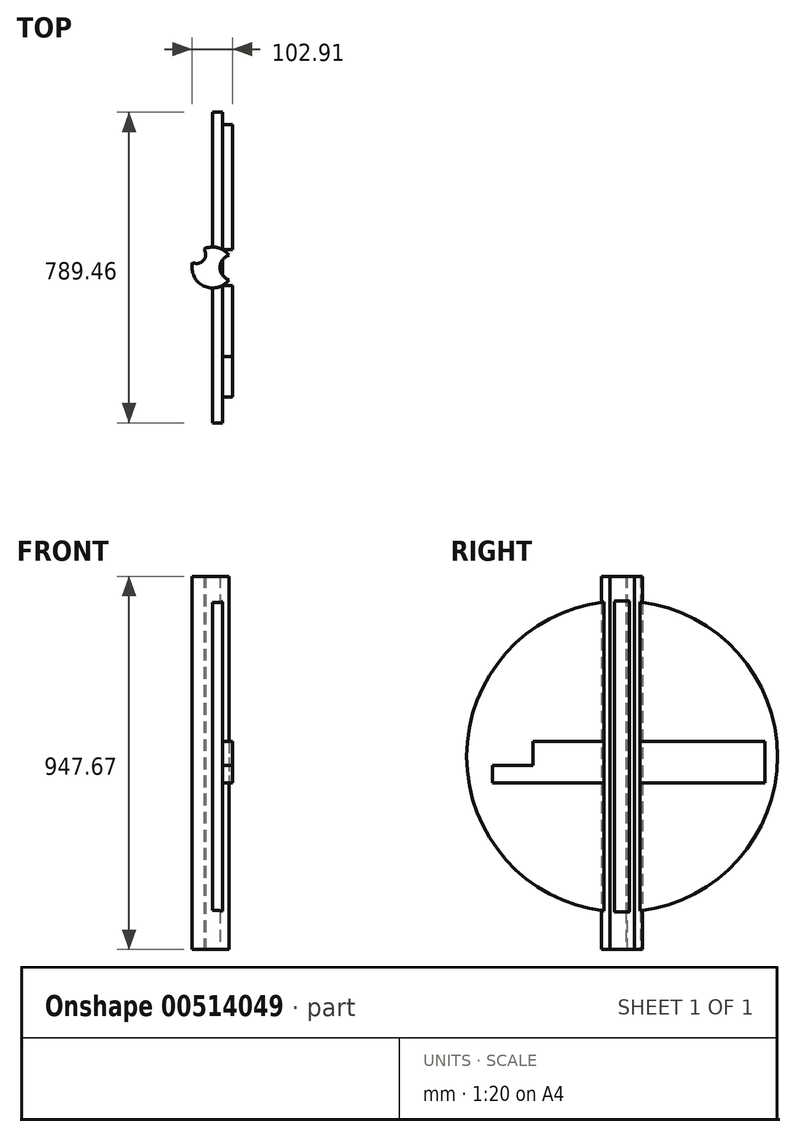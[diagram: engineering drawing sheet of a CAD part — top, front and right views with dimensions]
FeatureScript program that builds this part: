
annotation { "Feature Type Name" : "Feature", "Feature Type Description" : "" }
export const myFeature = defineFeature(function(context is Context, id is Id, definition is map)
    precondition{}
    {
        {
            var Q0;
            Q0=qCreatedBy(makeId("Top.planeOp"),FACE);
            var sketch = newSketch(context, id + "F0", { "sketchPlane" : qUnion([Q0])});
            skArc(sketch, "E0", {"start": v(-50.53, 12.73) * mm, "mid": v(-22.4, -47.04) * mm, "end": v(41.72, -31.21) * mm});
            skArc(sketch, "E1", {"start": v(41.72, 31.21) * mm, "mid": v(19.21, 0) * mm, "end": v(41.72, -31.21) * mm});
            skArc(sketch, "E2", {"start": v(-50.53, 12.73) * mm, "mid": v(-22.53, 18.59) * mm, "end": v(-22.09, 47.2) * mm});
            skArc(sketch, "E3.trimOffspring", {"start": v(41.72, 31.21) * mm, "mid": v(12.66, 50.55) * mm, "end": v(-22.09, 47.2) * mm});
            skSolve(sketch);
        }
        {
            var Q0;
            Q0=makeQuery(id+"F0.imprint","IMPRINT",FACE,{"disambiguationData":[TD([[makeQuery(id+"F0.imprint","IMPRINT",EDGE,{"derivedFrom":sQuery(id+"F0.wireOp",EDGE,"E0")}),1.0]])]});
            extrude(context, id + "F1", {"entities" : qUnion([Q0]), "depth" : 34.3 * mm, "offsetDistance" : 25.4 * mm});
        }
        {
            var Q0;
            Q0=makeQuery(id+"F1.opExtrude","CAP_FACE",FACE,{"disambiguationData":[OSD([sQuery(id+"F0.wireOp",EDGE,"E0"),sQuery(id+"F0.wireOp",EDGE,"E1"),sQuery(id+"F0.wireOp",EDGE,"E2"),sQuery(id+"F0.wireOp",EDGE,"E3.trimOffspring")])],"isStart":false});
            extrude(context, id + "F2", {"entities" : qUnion([Q0]), "operationType" : NewBodyOperationType.ADD, "depth" : 36.07 * mm, "offsetDistance" : 25.4 * mm});
        }
        {
            var Q0;
            Q0=makeQuery(id+"F2.opExtrude","CAP_FACE",FACE,{"disambiguationData":[OSD([sQuery(id+"F0.wireOp",EDGE,"E0"),sQuery(id+"F0.wireOp",EDGE,"E1"),sQuery(id+"F0.wireOp",EDGE,"E2"),sQuery(id+"F0.wireOp",EDGE,"E3.trimOffspring")])],"isStart":false});
            extrude(context, id + "F3", {"entities" : qUnion([Q0]), "operationType" : NewBodyOperationType.ADD, "depth" : 89.92 * mm, "offsetDistance" : 25.4 * mm});
        }
        {
            var Q0;
            Q0=makeQuery(id+"F3.opExtrude","CAP_FACE",FACE,{"disambiguationData":[OSD([sQuery(id+"F0.wireOp",EDGE,"E0"),sQuery(id+"F0.wireOp",EDGE,"E1"),sQuery(id+"F0.wireOp",EDGE,"E2"),sQuery(id+"F0.wireOp",EDGE,"E3.trimOffspring")])],"isStart":false});
            extrude(context, id + "F4", {"entities" : qUnion([Q0]), "operationType" : NewBodyOperationType.ADD, "depth" : 297.18 * mm, "offsetDistance" : 25.4 * mm});
        }
        {
            var Q0;
            Q0=makeQuery(id+"F1.opExtrude","CAP_FACE",FACE,{"disambiguationData":[OSD([sQuery(id+"F0.wireOp",EDGE,"E0"),sQuery(id+"F0.wireOp",EDGE,"E1"),sQuery(id+"F0.wireOp",EDGE,"E2"),sQuery(id+"F0.wireOp",EDGE,"E3.trimOffspring")])],"isStart":true});
            extrude(context, id + "F5", {"entities" : qUnion([Q0]), "operationType" : NewBodyOperationType.ADD, "depth" : 490.22 * mm, "offsetDistance" : 25.4 * mm});
        }
        {
            var Q0;
            Q0=qCreatedBy(makeId("Right.planeOp"),FACE);
            var sketch = newSketch(context, id + "F6", { "sketchPlane" : qUnion([Q0])});
            skLineSegment(sketch, "E4.bottom", {"start": v(-329.56, -22.24) * mm, "end": v(-226.5, -22.24) * mm});
            skLineSegment(sketch, "E4.top", {"start": v(-329.56, 37.68) * mm, "end": v(-226.5, 37.68) * mm});
            skLineSegment(sketch, "E4.left", {"start": v(-329.56, -22.24) * mm, "end": v(-329.56, 37.68) * mm});
            skLineSegment(sketch, "E4.right", {"start": v(-226.5, -22.24) * mm, "end": v(-226.5, 37.68) * mm});
            skLineSegment(sketch, "E5.bottom", {"start": v(-329.56, -22.24) * mm, "end": v(-329.56, -22.24) * mm});
            skLineSegment(sketch, "E5.top", {"start": v(-329.56, -67.78) * mm, "end": v(-329.56, -67.78) * mm});
            skLineSegment(sketch, "E5.left", {"start": v(-329.56, -22.24) * mm, "end": v(-329.56, -67.78) * mm});
            skLineSegment(sketch, "E5.right", {"start": v(-329.56, -22.24) * mm, "end": v(-329.56, -67.78) * mm});
            skLineSegment(sketch, "E6.bottom", {"start": v(-329.56, -67.78) * mm, "end": v(363.16, -67.78) * mm});
            skLineSegment(sketch, "E6.top", {"start": v(-329.56, 37.68) * mm, "end": v(363.16, 37.68) * mm});
            skLineSegment(sketch, "E6.left", {"start": v(-329.56, -67.78) * mm, "end": v(-329.56, 37.68) * mm});
            skLineSegment(sketch, "E6.right", {"start": v(363.16, -67.78) * mm, "end": v(363.16, 37.68) * mm});
            skSolve(sketch);
        }
        {
            var Q0;
            {var subQ4=sQuery(id+"F6.wireOp",EDGE,"E4.bottom");Q0=makeQuery(id+"F6.imprint","IMPRINT",FACE,{"disambiguationData":[TD([[makeQuery(id+"F6.imprint","IMPRINT",EDGE,{"derivedFrom":subQ4}),-1.0]])]});}
            extrude(context, id + "F7", {"entities" : qUnion([Q0]), "operationType" : NewBodyOperationType.ADD, "depth" : 25.4 * mm, "offsetDistance" : 25.4 * mm});
        }
        {
            var Q0;
            {var subQ0=sQuery(id+"F0.wireOp",EDGE,"E0");var subQ1=sQuery(id+"F6.wireOp",EDGE,"E6.top");var subQ2=sQuery(id+"F6.wireOp",EDGE,"E4.bottom");var subQ3=sQuery(id+"F6.wireOp",EDGE,"E6.left");var subQ4=sQuery(id+"F6.wireOp",EDGE,"E4.right");var subQ5=sQuery(id+"F6.wireOp",EDGE,"E6.bottom");Q0=makeQuery(id+"F7.boolean.opBoolean","SPLIT",FACE,{"disambiguationData":[TD([makeQuery(id+"F1.opExtrude","SWEPT_FACE",FACE,{"disambiguationData":[OSD([subQ0])]})])],"derivedFrom":makeQuery(id+"F7.opExtrude","CAP_FACE",FACE,{"disambiguationData":[OSD([subQ2,subQ4,subQ5,subQ1,subQ3,sQuery(id+"F6.wireOp",EDGE,"E6.right")])],"isStart":false})});}
            var Q1;
            {var subQ0=sQuery(id+"F0.wireOp",EDGE,"E3.trimOffspring");var subQ1=sQuery(id+"F6.wireOp",EDGE,"E6.bottom");var subQ2=sQuery(id+"F6.wireOp",EDGE,"E6.top");var subQ3=sQuery(id+"F6.wireOp",EDGE,"E6.right");Q1=makeQuery(id+"F7.boolean.opBoolean","SPLIT",FACE,{"disambiguationData":[TD([makeQuery(id+"F1.opExtrude","SWEPT_FACE",FACE,{"disambiguationData":[OSD([subQ0])]})])],"derivedFrom":makeQuery(id+"F7.opExtrude","CAP_FACE",FACE,{"disambiguationData":[OSD([sQuery(id+"F6.wireOp",EDGE,"E4.bottom"),sQuery(id+"F6.wireOp",EDGE,"E4.right"),subQ1,subQ2,sQuery(id+"F6.wireOp",EDGE,"E6.left"),subQ3])],"isStart":false})});}
            extrude(context, id + "F8", {"entities" : qUnion([Q0, Q1]), "operationType" : NewBodyOperationType.ADD, "depth" : 25.4 * mm, "offsetDistance" : 25.4 * mm});
        }
        {
            var Q0;
            Q0=qCreatedBy(makeId("Right.planeOp"),FACE);
            var sketch = newSketch(context, id + "F9", { "sketchPlane" : qUnion([Q0])});
            skCircle(sketch, "E7", {"center": v(0, 0) * mm, "radius": 267.1 * mm});
            skSolve(sketch);
        }
        {
            var Q0;
            Q0=makeQuery(id+"F9.imprint","IMPRINT",FACE,{"disambiguationData":[TD([[makeQuery(id+"F9.imprint","IMPRINT",EDGE,{"derivedFrom":sQuery(id+"F9.wireOp",EDGE,"E7")}),1.0]])]});
            extrude(context, id + "F10", {"entities" : qUnion([Q0]), "operationType" : NewBodyOperationType.ADD, "depth" : 25.4 * mm, "offsetDistance" : 25.4 * mm});
        }
        {
            var Q0;
            Q0=qCreatedBy(makeId("Right.planeOp"),FACE);
            var sketch = newSketch(context, id + "F11", { "sketchPlane" : qUnion([Q0])});
            skCircle(sketch, "E8", {"center": v(0, 0) * mm, "radius": 394.73 * mm});
            skSolve(sketch);
        }
        {
            var Q0;
            Q0=makeQuery(id+"F11.imprint","IMPRINT",FACE,{"disambiguationData":[TD([[makeQuery(id+"F11.imprint","IMPRINT",EDGE,{"derivedFrom":sQuery(id+"F11.wireOp",EDGE,"E8")}),1.0]])]});
            extrude(context, id + "F12", {"entities" : qUnion([Q0]), "operationType" : NewBodyOperationType.ADD, "depth" : 25.4 * mm, "offsetDistance" : 25.4 * mm});
        }
    });
